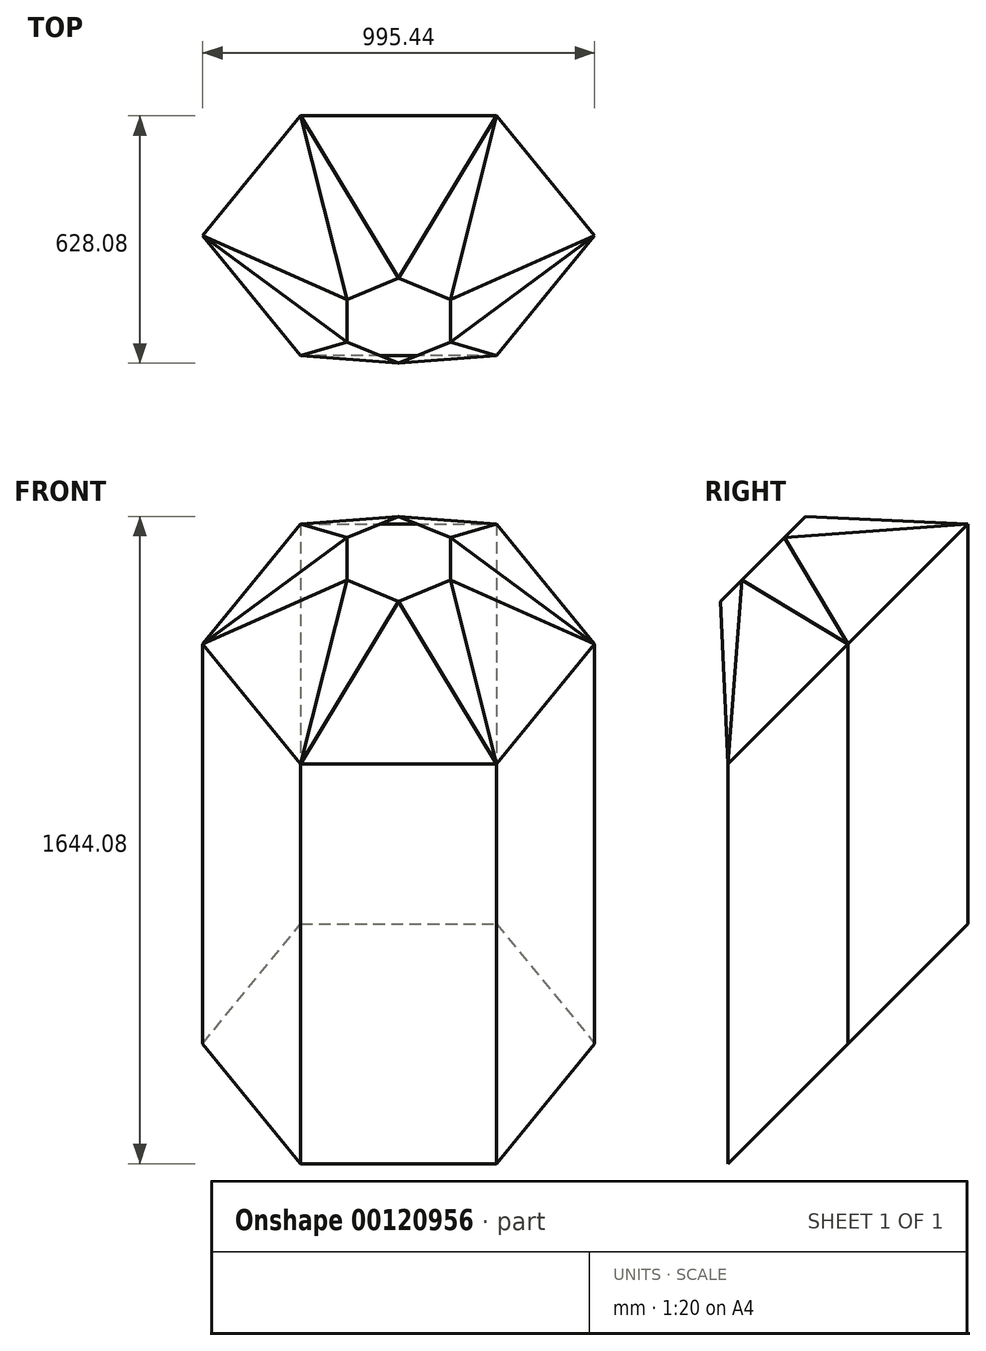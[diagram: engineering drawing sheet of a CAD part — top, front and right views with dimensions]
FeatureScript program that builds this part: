
annotation { "Feature Type Name" : "Feature", "Feature Type Description" : "" }
export const myFeature = defineFeature(function(context is Context, id is Id, definition is map)
    precondition{}
    {
        {
            var Q0;
            Q0=qCreatedBy(makeId("Top.planeOp"),FACE);
            var sketch = newSketch(context, id + "F0", { "sketchPlane" : qUnion([Q0])});
            skLineSegment(sketch, "E0", {"start": v(0, 0) * mm, "end": v(0, 304.8) * mm, "construction": true});
            skLineSegment(sketch, "E1", {"start": v(-304.8, 0) * mm, "end": v(304.8, 0) * mm, "construction": true});
            skSolve(sketch);
        }
        {
            var Q0;
            Q0=sQuery(id+"F0.wireOp",EDGE,"E1");
            cPlane(context, id + "F1", {"entities" : qUnion([Q0]), "cplaneType" : CPlaneType.LINE_ANGLE, "offset" : 25.4 * mm, "angle" : 135 * degree, "width" : 152.4 * mm, "height" : 152.4 * mm});
        }
        {
            var Q0;
            Q0=qCreatedBy(makeId("Front.planeOp"),FACE);
            var sketch = newSketch(context, id + "F2", { "sketchPlane" : qUnion([Q0])});
            skLineSegment(sketch, "E2", {"start": v(0, 0) * mm, "end": v(0, -1016) * mm, "construction": true});
            skLineSegment(sketch, "E3", {"start": v(304.8, -1016) * mm, "end": v(-304.8, -1016) * mm, "construction": true});
            skSolve(sketch);
        }
        {
            var Q0;
            Q0=sQuery(id+"F2.wireOp",EDGE,"E3");
            cPlane(context, id + "F3", {"entities" : qUnion([Q0]), "cplaneType" : CPlaneType.LINE_ANGLE, "offset" : 25.4 * mm, "angle" : 45 * degree, "width" : 152.4 * mm, "height" : 152.4 * mm});
        }
        {
            var Q0;
            Q0=qCreatedBy(id+"F1.planeOp",FACE);
            var sketch = newSketch(context, id + "F4", { "sketchPlane" : qUnion([Q0])});
            skLineSegment(sketch, "E4", {"start": v(0, 0) * mm, "end": v(0, 431.04) * mm, "construction": true});
            skCircle(sketch, "E5.cCircle", {"center": v(0, 0) * mm, "radius": 431.04 * mm, "construction": true});
            skLineSegment(sketch, "E5.0", {"start": v(-248.86, 431.04) * mm, "end": v(248.86, 431.04) * mm});
            skLineSegment(sketch, "E5.1", {"start": v(248.86, 431.04) * mm, "end": v(497.72, 0) * mm});
            skLineSegment(sketch, "E5.2", {"start": v(497.72, 0) * mm, "end": v(248.86, -431.04) * mm});
            skLineSegment(sketch, "E5.3", {"start": v(248.86, -431.04) * mm, "end": v(-248.86, -431.04) * mm});
            skLineSegment(sketch, "E5.4", {"start": v(-248.86, -431.04) * mm, "end": v(-497.72, 0) * mm});
            skLineSegment(sketch, "E5.5", {"start": v(-497.72, 0) * mm, "end": v(-248.86, 431.04) * mm});
            skPoint(sketch, "E5.0.midPoint", {"position": v(0, 431.04) * mm});
            skSolve(sketch);
        }
        {
            var Q0;
            Q0=qCreatedBy(id+"F3.planeOp",FACE);
            var sketch = newSketch(context, id + "F5", { "sketchPlane" : qUnion([Q0])});
            skPoint(sketch, "E6.0", {"position": v(0, -718.42) * mm});
            skLineSegment(sketch, "E7", {"start": v(0, -718.42) * mm, "end": v(0, -287.38) * mm, "construction": true});
            skCircle(sketch, "E8.cCircle", {"center": v(0, -718.42) * mm, "radius": 431.04 * mm, "construction": true});
            skLineSegment(sketch, "E8.0", {"start": v(-248.86, -287.38) * mm, "end": v(248.86, -287.38) * mm});
            skLineSegment(sketch, "E8.1", {"start": v(248.86, -287.38) * mm, "end": v(497.72, -718.42) * mm});
            skLineSegment(sketch, "E8.2", {"start": v(497.72, -718.42) * mm, "end": v(248.86, -1149.46) * mm});
            skLineSegment(sketch, "E8.3", {"start": v(248.86, -1149.46) * mm, "end": v(-248.86, -1149.46) * mm});
            skLineSegment(sketch, "E8.4", {"start": v(-248.86, -1149.46) * mm, "end": v(-497.72, -718.42) * mm});
            skLineSegment(sketch, "E8.5", {"start": v(-497.72, -718.42) * mm, "end": v(-248.86, -287.38) * mm});
            skPoint(sketch, "E8.0.midPoint", {"position": v(0, -287.38) * mm});
            skSolve(sketch);
        }
        {
            var Q0;
            Q0=makeQuery(id+"F4.imprint","IMPRINT",FACE,{"disambiguationData":[TD([[makeQuery(id+"F4.imprint","IMPRINT",EDGE,{"derivedFrom":sQuery(id+"F4.wireOp",EDGE,"E5.0")}),-1.0]])]});
            var Q1;
            Q1=makeQuery(id+"F5.imprint","IMPRINT",FACE,{"disambiguationData":[TD([[makeQuery(id+"F5.imprint","IMPRINT",EDGE,{"derivedFrom":sQuery(id+"F5.wireOp",EDGE,"E8.0")}),-1.0]])]});
            var Q2;
            Q2=makeQuery(id+"F4.imprint","IMPRINT",FACE,{"disambiguationData":[TD([[makeQuery(id+"F4.imprint","IMPRINT",EDGE,{"derivedFrom":sQuery(id+"F4.wireOp",EDGE,"E5.0")}),-1.0]])]});
            var Q3;
            Q3=makeQuery(id+"F5.imprint","IMPRINT",FACE,{"disambiguationData":[TD([[makeQuery(id+"F5.imprint","IMPRINT",EDGE,{"derivedFrom":sQuery(id+"F5.wireOp",EDGE,"E8.0")}),-1.0]])]});
            loft(context, id + "F6", {"bodyType" : ToolBodyType.SURFACE, "sheetProfilesArray" : [{ "sheetProfileEntities" : qUnion([Q0]) }, { "sheetProfileEntities" : qUnion([Q1]) }], "wireProfilesArray" : [{ "wireProfileEntities" : qUnion([Q2]) }, { "wireProfileEntities" : qUnion([Q3]) }]});
        }
        {
            var Q0;
            Q0=qCreatedBy(id+"F1.planeOp",FACE);
            cPlane(context, id + "F7", {"entities" : qUnion([Q0]), "cplaneType" : CPlaneType.OFFSET, "offset" : 304.8 * mm, "width" : 152.4 * mm, "height" : 152.4 * mm});
        }
        {
            var Q0;
            Q0=qCreatedBy(id+"F7.planeOp",FACE);
            var sketch = newSketch(context, id + "F8", { "sketchPlane" : qUnion([Q0])});
            skCircle(sketch, "E9.cCircle", {"center": v(0, 0) * mm, "radius": 131.98 * mm, "construction": true});
            skLineSegment(sketch, "E9.0", {"start": v(131.98, 76.2) * mm, "end": v(131.98, -76.2) * mm});
            skLineSegment(sketch, "E9.1", {"start": v(131.98, -76.2) * mm, "end": v(0, -152.4) * mm});
            skLineSegment(sketch, "E9.2", {"start": v(0, -152.4) * mm, "end": v(-131.98, -76.2) * mm});
            skLineSegment(sketch, "E9.3", {"start": v(-131.98, -76.2) * mm, "end": v(-131.98, 76.2) * mm});
            skLineSegment(sketch, "E9.4", {"start": v(-131.98, 76.2) * mm, "end": v(0, 152.4) * mm});
            skLineSegment(sketch, "E9.5", {"start": v(0, 152.4) * mm, "end": v(131.98, 76.2) * mm});
            skPoint(sketch, "E9.0.midPoint", {"position": v(131.98, 0) * mm});
            skSolve(sketch);
        }
        {
            var Q0;
            Q0=sQuery(id+"F8.wireOp",VERTEX,"E9.0.end");
            var Q1;
            Q1=sQuery(id+"F4.wireOp",EDGE,"E5.2");
            loft(context, id + "F9", {"bodyType" : ToolBodyType.SURFACE, "wireProfilesArray" : [{ "wireProfileEntities" : qUnion([Q0]) }, { "wireProfileEntities" : qUnion([Q1]) }]});
        }
        {
            var Q0;
            Q0=sQuery(id+"F8.wireOp",EDGE,"E9.0");
            var Q1;
            Q1=sQuery(id+"F4.wireOp",VERTEX,"E5.1.end");
            loft(context, id + "F10", {"bodyType" : ToolBodyType.SURFACE, "wireProfilesArray" : [{ "wireProfileEntities" : qUnion([Q0]) }, { "wireProfileEntities" : qUnion([Q1]) }]});
        }
        {
            var Q0;
            Q0=qCreatedBy(makeId("Right.planeOp"),FACE);
            var sketch = newSketch(context, id + "F11", { "sketchPlane" : qUnion([Q0])});
            skPoint(sketch, "E10.0", {"position": v(-215.53, 215.53) * mm});
            skLineSegment(sketch, "E11", {"start": v(0, 0) * mm, "end": v(-215.53, 215.53) * mm, "construction": true});
            skSolve(sketch);
        }
        {
            var Q0;
            Q0=makeQuery(id+"F10.opLoft","SWEPT_BODY",BODY,{"disambiguationData":[OSD([sQuery(id+"F4.wireOp",VERTEX,"E5.1.end"),sQuery(id+"F8.wireOp",EDGE,"E9.0")])]});
            var Q1;
            Q1=makeQuery(id+"F9.opLoft","SWEPT_BODY",BODY,{"disambiguationData":[OSD([sQuery(id+"F4.wireOp",EDGE,"E5.2"),sQuery(id+"F8.wireOp",VERTEX,"E9.0.end")])]});
            var Q2;
            Q2=sQuery(id+"F11.wireOp",EDGE,"E11");
            circularPattern(context, id + "F12", {"entities" : qUnion([Q0, Q1]), "axis" : qUnion([Q2]), "angle" : 360 * degree, "instanceCount" : 6, "equalSpace" : true});
        }
    });
